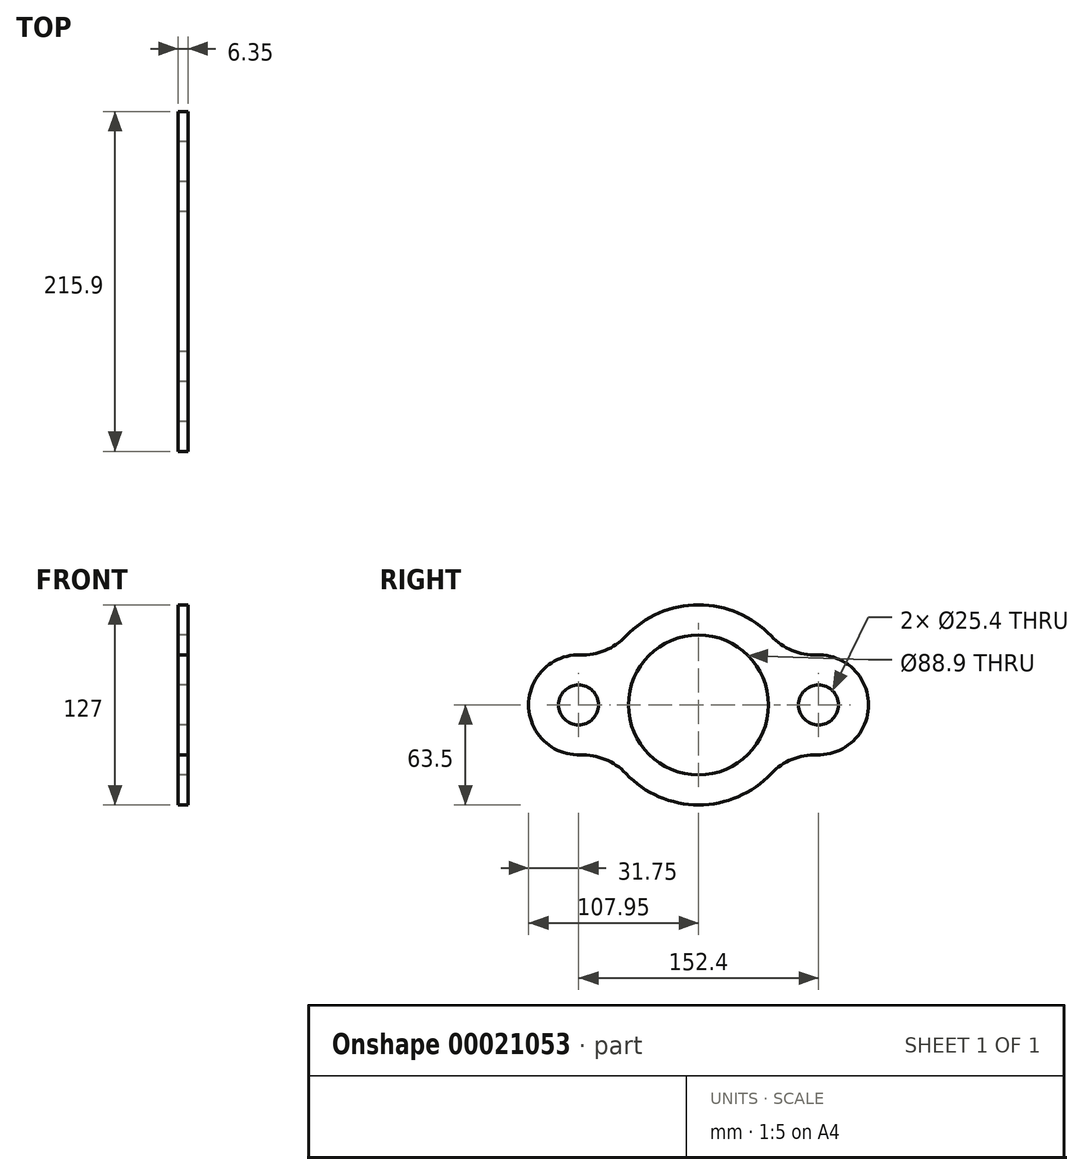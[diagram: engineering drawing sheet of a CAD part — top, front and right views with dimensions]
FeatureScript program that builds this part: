
annotation { "Feature Type Name" : "Feature", "Feature Type Description" : "" }
export const myFeature = defineFeature(function(context is Context, id is Id, definition is map)
    precondition{}
    {
        {
            var Q0;
            Q0=qCreatedBy(makeId("Right.planeOp"),FACE);
            var sketch = newSketch(context, id + "F0", { "sketchPlane" : qUnion([Q0])});
            skCircle(sketch, "E0", {"center": v(0, 0) * mm, "radius": 44.45 * mm});
            skArc(sketch, "E1", {"start": v(-46.14, -43.63) * mm, "mid": v(0, -63.5) * mm, "end": v(46.14, -43.63) * mm});
            skLineSegment(sketch, "E2", {"start": v(-116.98, 0) * mm, "end": v(107.95, 0) * mm, "construction": true});
            skCircle(sketch, "E3", {"center": v(-76.2, 0) * mm, "radius": 12.7 * mm});
            skCircle(sketch, "E4", {"center": v(76.2, 0) * mm, "radius": 12.7 * mm});
            skArc(sketch, "E5", {"start": v(-75.12, 31.73) * mm, "mid": v(-107.95, 0) * mm, "end": v(-75.12, -31.73) * mm});
            skArc(sketch, "E6", {"start": v(75.12, -31.73) * mm, "mid": v(107.95, 0) * mm, "end": v(75.12, 31.73) * mm});
            skArc(sketch, "E7.trimOffspring", {"start": v(46.14, 43.63) * mm, "mid": v(0, 63.5) * mm, "end": v(-46.14, 43.63) * mm});
            skPoint(sketch, "E8.visualSharp", {"position": v(-57.94, 25.98) * mm});
            skArc(sketch, "E8.filletArc", {"start": v(-75.12, 31.73) * mm, "mid": v(-59.35, 34.56) * mm, "end": v(-46.14, 43.63) * mm});
            skPoint(sketch, "E9.visualSharp", {"position": v(57.94, 25.98) * mm});
            skArc(sketch, "E9.filletArc", {"start": v(46.14, 43.63) * mm, "mid": v(59.35, 34.56) * mm, "end": v(75.12, 31.73) * mm});
            skPoint(sketch, "E10.visualSharp", {"position": v(-57.94, -25.98) * mm});
            skArc(sketch, "E10.filletArc", {"start": v(-46.14, -43.63) * mm, "mid": v(-59.35, -34.56) * mm, "end": v(-75.12, -31.73) * mm});
            skPoint(sketch, "E11.visualSharp", {"position": v(57.94, -25.98) * mm});
            skArc(sketch, "E11.filletArc", {"start": v(75.12, -31.73) * mm, "mid": v(59.35, -34.56) * mm, "end": v(46.14, -43.63) * mm});
            skLineSegment(sketch, "E12", {"start": v(0, 0) * mm, "end": v(0, 63.5) * mm, "construction": true});
            skSolve(sketch);
        }
        {
            var Q0;
            Q0 = qSketchRegion(id + "F0", true);
            extrude(context, id + "F1", {"entities" : qUnion([Q0]), "depth" : 6.35 * mm});
        }
    });
